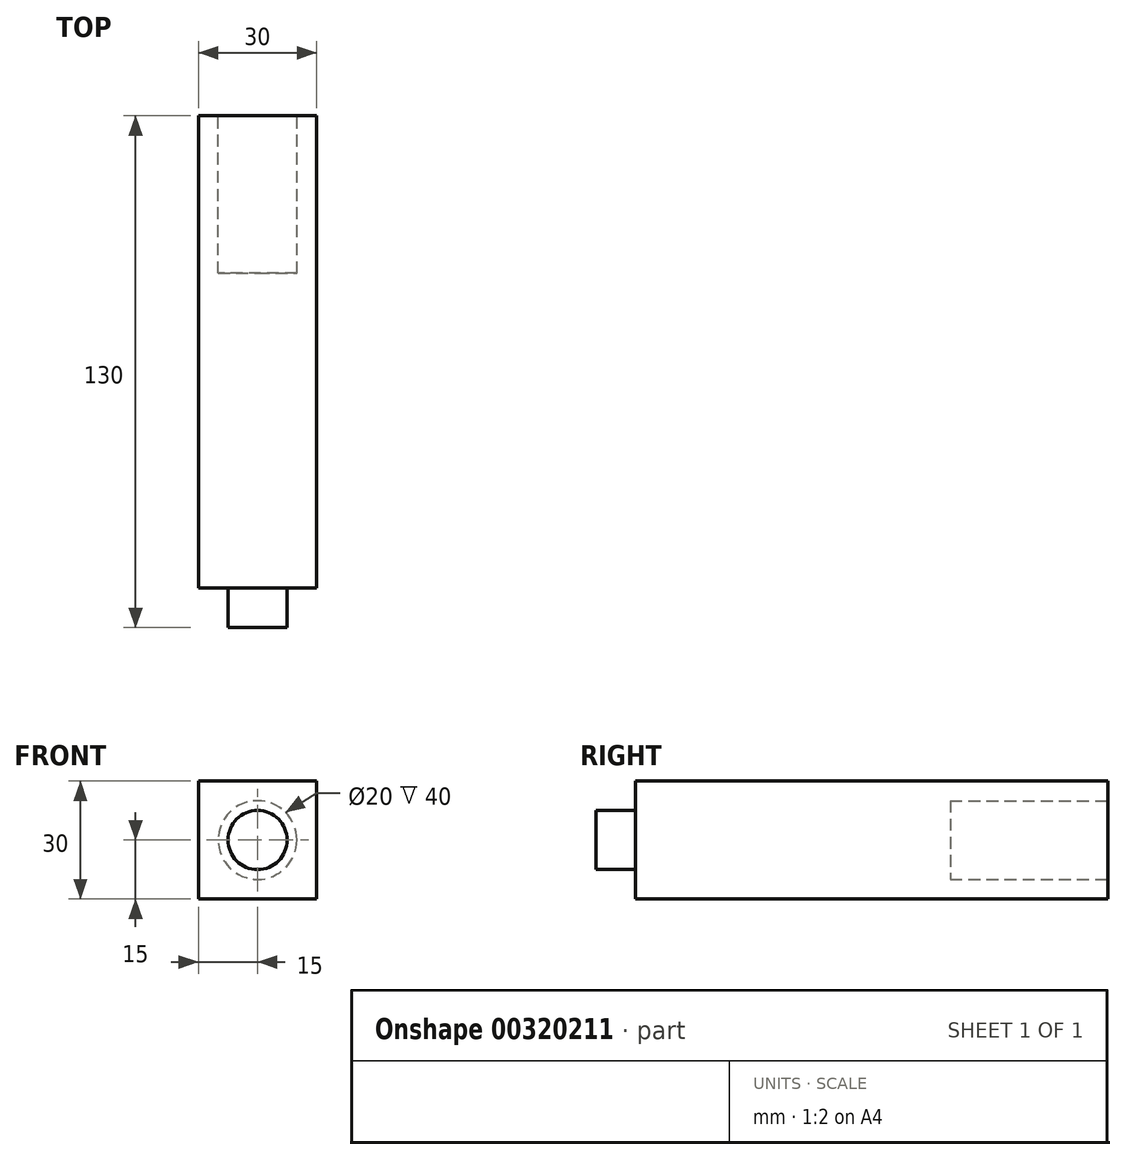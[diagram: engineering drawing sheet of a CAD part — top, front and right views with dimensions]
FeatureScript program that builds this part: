
annotation { "Feature Type Name" : "Feature", "Feature Type Description" : "" }
export const myFeature = defineFeature(function(context is Context, id is Id, definition is map)
    precondition{}
    {
        {
            var Q0;
            Q0=qCreatedBy(makeId("Front.planeOp"),FACE);
            var sketch = newSketch(context, id + "F0", { "sketchPlane" : qUnion([Q0])});
            skPoint(sketch, "E0.orphan", {"position": v(-15, 0) * mm});
            skLineSegment(sketch, "E1", {"start": v(15, 0) * mm, "end": v(15, 15) * mm});
            skLineSegment(sketch, "E2", {"start": v(15, 15) * mm, "end": v(0, 15) * mm});
            skLineSegment(sketch, "E3", {"start": v(-15, 15) * mm, "end": v(-15, -15) * mm});
            skLineSegment(sketch, "E4", {"start": v(-15, -15) * mm, "end": v(15, -15) * mm});
            skLineSegment(sketch, "E5", {"start": v(15, -15) * mm, "end": v(15, 0) * mm});
            skLineSegment(sketch, "E6", {"start": v(-15, 15) * mm, "end": v(0, 15) * mm});
            skSolve(sketch);
        }
        {
            var Q0;
            Q0 = qSketchRegion(id + "F0", true);
            extrude(context, id + "F1", {"entities" : qUnion([Q0]), "endBound" : BoundingType.SYMMETRIC, "depth" : 120 * mm});
        }
        {
            var Q0;
            Q0=makeQuery(id+"F1.opExtrude","CAP_FACE",FACE,{"disambiguationData":[OSD([sQuery(id+"F0.wireOp",EDGE,"E1"),sQuery(id+"F0.wireOp",EDGE,"E2"),sQuery(id+"F0.wireOp",EDGE,"E3"),sQuery(id+"F0.wireOp",EDGE,"E4"),sQuery(id+"F0.wireOp",EDGE,"E5"),sQuery(id+"F0.wireOp",EDGE,"E6")])],"isStart":false});
            var sketch = newSketch(context, id + "F2", { "sketchPlane" : qUnion([Q0])});
            skCircle(sketch, "E7", {"center": v(0, 0) * mm, "radius": 7.5 * mm});
            skSolve(sketch);
        }
        {
            var Q0;
            Q0 = qSketchRegion(id + "F2", true);
            extrude(context, id + "F3", {"entities" : qUnion([Q0]), "operationType" : NewBodyOperationType.ADD, "depth" : 10 * mm});
        }
        {
            var Q0;
            Q0=makeQuery(id+"F1.opExtrude","CAP_FACE",FACE,{"disambiguationData":[OSD([sQuery(id+"F0.wireOp",EDGE,"E1"),sQuery(id+"F0.wireOp",EDGE,"E2"),sQuery(id+"F0.wireOp",EDGE,"E3"),sQuery(id+"F0.wireOp",EDGE,"E4"),sQuery(id+"F0.wireOp",EDGE,"E5"),sQuery(id+"F0.wireOp",EDGE,"E6")])],"isStart":true});
            var sketch = newSketch(context, id + "F4", { "sketchPlane" : qUnion([Q0])});
            skCircle(sketch, "E8", {"center": v(0, 0) * mm, "radius": 10 * mm});
            skSolve(sketch);
        }
        {
            var Q0;
            Q0 = qSketchRegion(id + "F4", true);
            extrude(context, id + "F5", {"entities" : qUnion([Q0]), "operationType" : NewBodyOperationType.REMOVE, "oppositeDirection" : true, "depth" : 40 * mm});
        }
    });
